# Revit family: PRD_AR_TpsAndWtrSpplOtltFttngs_FittingUnit_AQFU0221-AQFU0225 2
name_source: partatom
category: Plumbing Fixtures
units: mm (PartAtom-declared; Revit-internal decimal feet)

## family parameters
Cut with Voids When Loaded = No
Enable Cutting in Views = No
Host = Face
Maintain Annotation Orientation = No
OmniClass Number = 23.45.55.11
OmniClass Title = Sanitary Components
Part Type = Normal
Room Calculation Point = No
Round Connector Dimension = Use Diameter
Shared = No

## types (5) — shared parameters
AssetType = Fixed
BodyMaterial = PRD_AR_StainlessSteel_SatinFinished
Category = Pr_40_20_87, Taps and water supply outlet fittings
Circulation = no
Default Elevation = 1050 mm
Export Type to IFC As = IfcDistributionChamberElementType
Finish = satin finished
Fitting = separately
FlowColdWater = 0.0 L/s
FlowHotWater = 0.0 L/s
HygieneFlushing = no
IfcExportAs = IfcDistributionChamberElement
IfcExportType = USERDEFINED
InletConversionSize = 20  [stored 0.0656168 ft]
InletSize = G 3/4
Manufacturer = KWC Group Management AG
ManufacturerName = KWC Group Management AG
ManufacturerURL = www.kwc-professional.com
Material = stainless steel
NominalDepth = 72 mm  [stored 0.23622 ft]
NominalHeight = 173 mm  [stored 0.567585 ft]
OutletSize = 15  [stored 0.0492126 ft]
OverallDepth = 72 mm
OverallHeight = 173 mm
PositionOfWaterConnection = from backside
ProductInformation = http://pim.kwc.com
Status = New
Type IFC Predefined Type = USERDEFINED
TypeOfMixing = yes
TypeOfMounting = wall mounting
URL = www.kwc-professional.com
Uniclass2015Code = Pr_40_20_87
Uniclass2015Title = Taps and water supply outlet fittings
Uniclass2015Version = Products v1.38
Version = 1
WashPlaceWidth = 700 mm

## per-type parameters (varying)
| type | BIMObjectName | Description | Features | HalfWidth | ModelNumber | Name | NominalWidth | NumberOfWashPlaces | OverallWidth | Size | Width |
| AQFU0221 | PRD_AR_TapsAndWaterSupplyOutletFittings_FittingUnit_AQFU0221 | Fitting unit ready for connection with 2 wash places, for wall mounting, for connection to hot and cold water from right or left at rear. Housing made of stainless steel, satin finished with pre-assembled fitting connection blocks and connection options for power supply to electronic fittings, stainless steel piping, hanging rail and mounting materials. | With 2 wash places, housing width 1400 mm. Wash place width 700 mm. | 700 mm  [stored 2.29659 ft] | 2030064904 | Fitting unit for wall mounting AQFU0221 | 1400 mm  [stored 4.59318 ft] | 2 | 1,400 mm | 1400 x 173 x 72 mm (W x H x D) | 1400 mm  [stored 4.59318 ft] |
| AQFU0222 | PRD_AR_TapsAndWaterSupplyOutletFittings_FittingUnit_AQFU0222 | Fitting unit ready for connection with 3 wash places, for wall mounting, for connection to hot and cold water from right or left at rear. Housing made of stainless steel, satin finished with pre-assembled fitting connection blocks and connection options for power supply to electronic fittings, stainless steel piping, hanging rail and mounting materials. | With 3 wash places, housing width 2100 mm. Wash place width 700 mm. | 1050 mm | 2030064903 | Fitting unit for wall mounting AQFU0222 | 2100 mm | 3 | 2,100 mm | 2100 x 173 x 72 mm (W x H x D) | 2100 mm |
| AQFU0223 | PRD_AR_TapsAndWaterSupplyOutletFittings_FittingUnit_AQFU0223 | Fitting unit ready for connection with 4 wash places, for wall mounting, for connection to hot and cold water from right or left at rear. Housing made of stainless steel, satin finished with pre-assembled fitting connection blocks and connection options for power supply to electronic fittings, stainless steel piping, hanging rail and mounting materials. | With 4 wash places, housing width 2800 mm. Wash place width 700 mm. | 1400 mm  [stored 4.59318 ft] | 2030064907 | Fitting unit for wall mounting AQFU0223 | 2800 mm  [stored 9.18635 ft] | 4 | 2,800 mm | 2800 x 173 x 72 mm (W x H x D) | 2800 mm  [stored 9.18635 ft] |
| AQFU0224 | PRD_AR_TapsAndWaterSupplyOutletFittings_FittingUnit_AQFU0224 | Fitting unit ready for connection with 5 wash places, for wall mounting, for connection to hot and cold water from right or left at rear. Housing made of stainless steel, satin finished with pre-assembled fitting connection blocks and connection options for power supply to electronic fittings, stainless steel piping, hanging rail and mounting materials. | With 5 wash places, housing width 3500 mm. Wash place width 700 mm. | 1750 mm  [stored 5.74147 ft] | 2030064912 | Fitting unit for wall mounting AQFU0224 | 3500 mm  [stored 11.4829 ft] | 5 | 3,500 mm | 3500 x 173 x 72 mm (W x H x D) | 3500 mm  [stored 11.4829 ft] |
| AQFU0225 | PRD_AR_TapsAndWaterSupplyOutletFittings_FittingUnit_AQFU0225 | Fitting unit ready for connection with 6 wash places, for wall mounting, for connection to hot and cold water from right or left at rear. Housing made of stainless steel, satin finished with pre-assembled fitting connection blocks and connection options for power supply to electronic fittings, stainless steel piping, hanging rail and mounting materials. | With 6 wash places, housing width 4200 mm. Wash place width 700 mm. | 2100 mm | 2030064917 | Fitting unit for wall mounting AQFU0225 | 4200 mm | 6 | 4,200 mm | 4200 x 173 x 72 mm (W x H x D) | 4200 mm |

note: column(s) folded — value = type name in every type: Model, ModelReference

note: [stored X ft] marks values corroborated as IEEE doubles in the binary element streams (Revit-internal decimal feet)

## geometry (parser evidence)
native form markers: Sweep x6
no freeform markers — native parametric forms only
